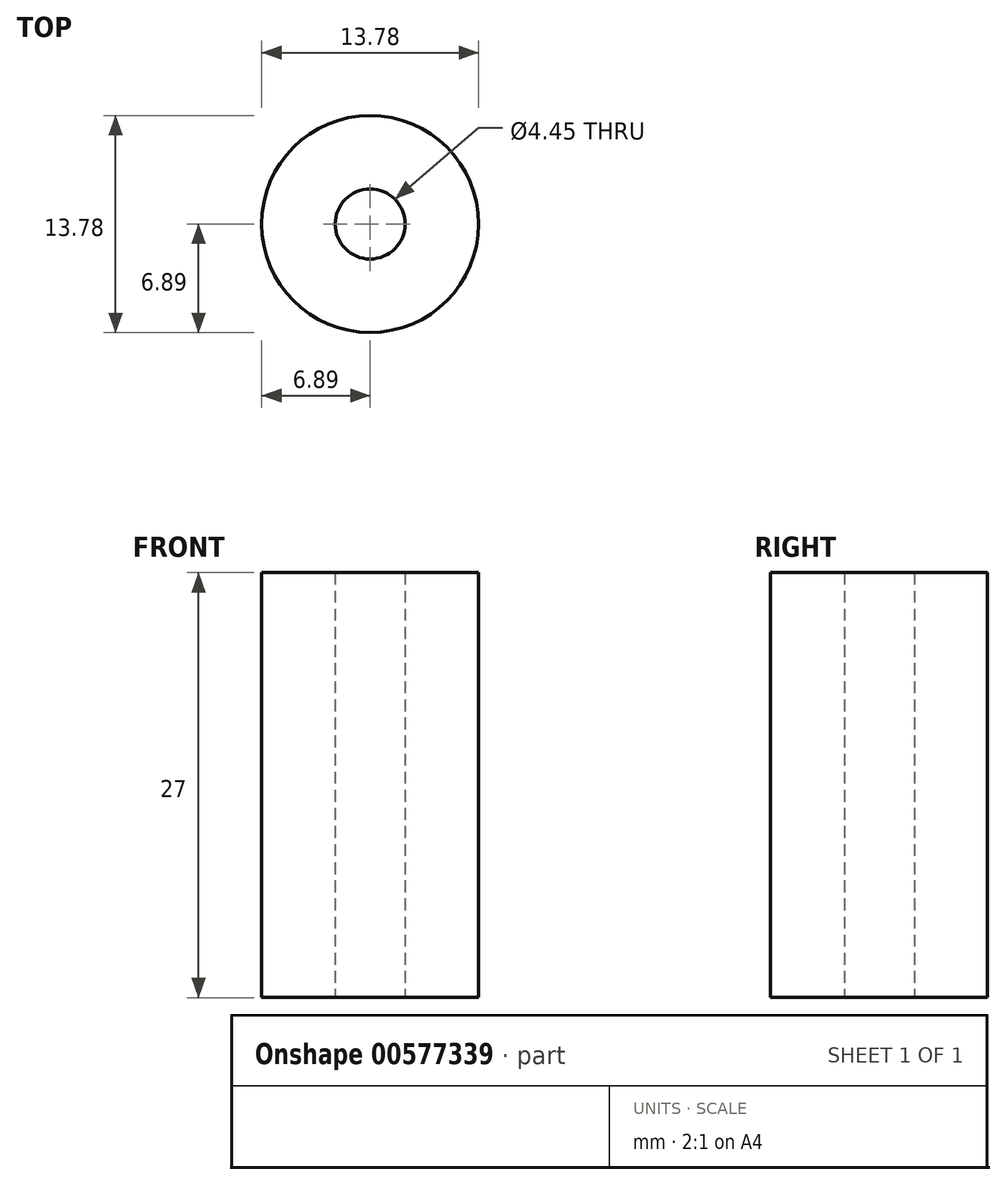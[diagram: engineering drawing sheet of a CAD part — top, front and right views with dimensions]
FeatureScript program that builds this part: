
annotation { "Feature Type Name" : "Feature", "Feature Type Description" : "" }
export const myFeature = defineFeature(function(context is Context, id is Id, definition is map)
    precondition{}
    {
        {
            var Q0;
            Q0=qCreatedBy(makeId("Top.planeOp"),FACE);
            var sketch = newSketch(context, id + "F0", { "sketchPlane" : qUnion([Q0])});
            skCircle(sketch, "E0", {"center": v(0, 0) * mm, "radius": 6.89 * mm});
            skCircle(sketch, "E1", {"center": v(0, 0) * mm, "radius": 2.22 * mm});
            skSolve(sketch);
        }
        {
            var Q0;
            Q0 = qSketchRegion(id + "F0", true);
            extrude(context, id + "F1", {"entities" : qUnion([Q0]), "endBound" : BoundingType.SYMMETRIC, "depth" : 27 * mm, "offsetDistance" : 25.4 * mm});
        }
    });
